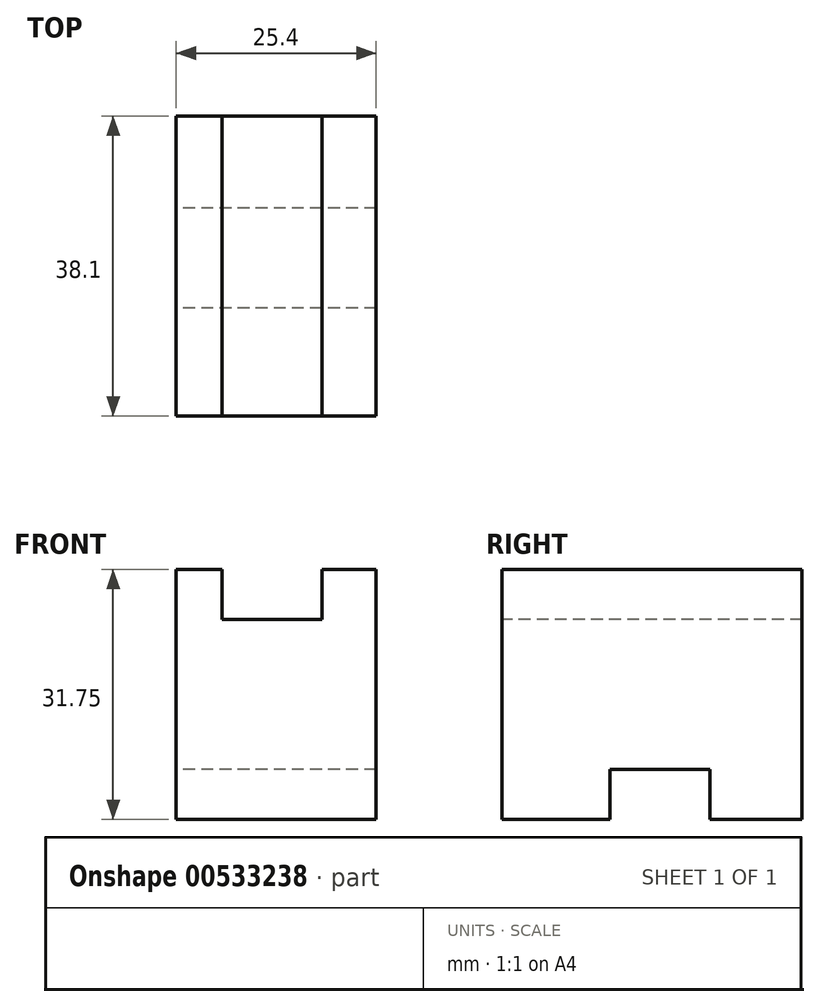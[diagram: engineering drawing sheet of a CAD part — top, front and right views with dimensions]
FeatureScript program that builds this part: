
annotation { "Feature Type Name" : "Feature", "Feature Type Description" : "" }
export const myFeature = defineFeature(function(context is Context, id is Id, definition is map)
    precondition{}
    {
        {
            var Q0;
            Q0=qCreatedBy(makeId("Front.planeOp"),FACE);
            var sketch = newSketch(context, id + "F0", { "sketchPlane" : qUnion([Q0])});
            skLineSegment(sketch, "E0", {"start": v(-40.82, 37.4) * mm, "end": v(-40.82, 5.65) * mm});
            skLineSegment(sketch, "E1", {"start": v(-40.82, 5.65) * mm, "end": v(-15.42, 5.65) * mm});
            skLineSegment(sketch, "E2", {"start": v(-15.42, 37.4) * mm, "end": v(-15.42, 5.65) * mm});
            skLineSegment(sketch, "E3", {"start": v(-40.82, 37.4) * mm, "end": v(-15.42, 37.4) * mm});
            skSolve(sketch);
        }
        {
            var Q0;
            Q0=makeQuery(id+"F0.imprint","IMPRINT",FACE,{"disambiguationData":[TD([[makeQuery(id+"F0.imprint","IMPRINT",EDGE,{"derivedFrom":sQuery(id+"F0.wireOp",EDGE,"E0")}),1.0]])]});
            extrude(context, id + "F1", {"entities" : qUnion([Q0]), "depth" : 38.1 * mm, "offsetDistance" : 25.4 * mm});
        }
        {
            var Q0;
            Q0=makeQuery(id+"F1.opExtrude","CAP_FACE",FACE,{"disambiguationData":[OSD([sQuery(id+"F0.wireOp",EDGE,"E0"),sQuery(id+"F0.wireOp",EDGE,"E1"),sQuery(id+"F0.wireOp",EDGE,"E2"),sQuery(id+"F0.wireOp",EDGE,"E3")])],"isStart":false});
            var sketch = newSketch(context, id + "F2", { "sketchPlane" : qUnion([Q0])});
            skLineSegment(sketch, "E4", {"start": v(-34.97, 37.4) * mm, "end": v(-34.97, 31.05) * mm});
            skLineSegment(sketch, "E5", {"start": v(-34.97, 31.05) * mm, "end": v(-22.27, 31.05) * mm});
            skLineSegment(sketch, "E6", {"start": v(-22.27, 31.05) * mm, "end": v(-22.27, 37.4) * mm});
            skSolve(sketch);
        }
        {
            var Q0;
            {var subQ0=sQuery(id+"F2.wireOp",EDGE,"E4");Q0=makeQuery(id+"F2.imprint","IMPRINT",FACE,{"disambiguationData":[TD([[makeQuery(id+"F2.imprint","IMPRINT",EDGE,{"derivedFrom":subQ0}),1.0]])]});}
            extrude(context, id + "F3", {"entities" : qUnion([Q0]), "operationType" : NewBodyOperationType.REMOVE, "oppositeDirection" : true, "depth" : 38.1 * mm, "offsetDistance" : 25.4 * mm});
        }
        {
            var Q0;
            Q0=makeQuery(id+"F1.opExtrude","SWEPT_FACE",FACE,{"disambiguationData":[OSD([sQuery(id+"F0.wireOp",EDGE,"E0")])]});
            var sketch = newSketch(context, id + "F4", { "sketchPlane" : qUnion([Q0])});
            skLineSegment(sketch, "E7", {"start": v(11.67, 5.65) * mm, "end": v(11.67, 12) * mm});
            skLineSegment(sketch, "E8", {"start": v(11.67, 12) * mm, "end": v(24.37, 12) * mm});
            skLineSegment(sketch, "E9", {"start": v(24.37, 12) * mm, "end": v(24.37, 5.65) * mm});
            skSolve(sketch);
        }
        {
            var Q0;
            {var subQ0=sQuery(id+"F4.wireOp",EDGE,"E7");Q0=makeQuery(id+"F4.imprint","IMPRINT",FACE,{"disambiguationData":[TD([[makeQuery(id+"F4.imprint","IMPRINT",EDGE,{"derivedFrom":subQ0}),-1.0]])]});}
            extrude(context, id + "F5", {"entities" : qUnion([Q0]), "operationType" : NewBodyOperationType.REMOVE, "oppositeDirection" : true, "depth" : 25.4 * mm, "offsetDistance" : 25.4 * mm});
        }
    });
